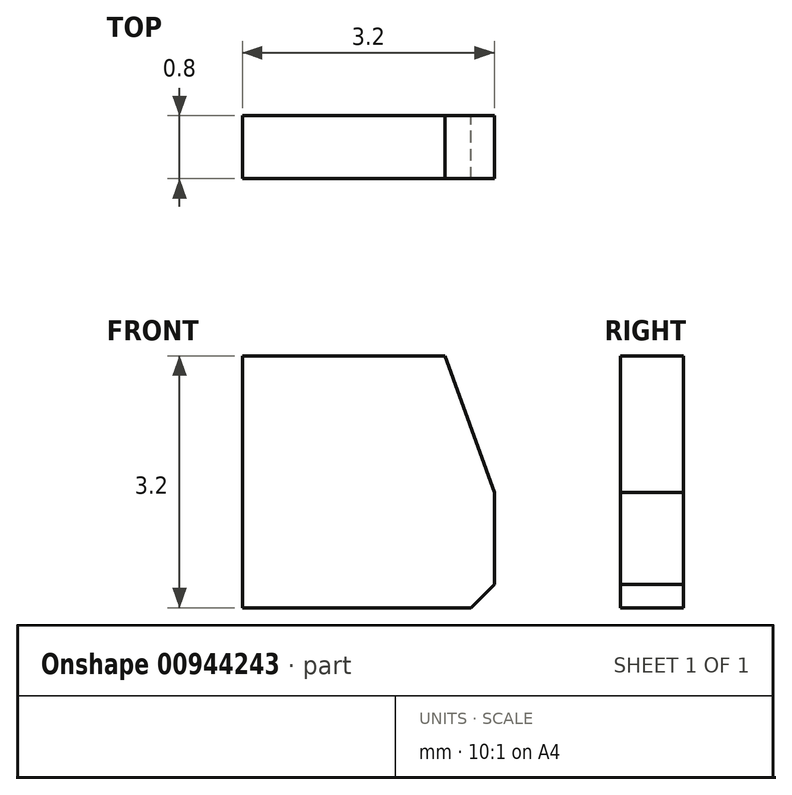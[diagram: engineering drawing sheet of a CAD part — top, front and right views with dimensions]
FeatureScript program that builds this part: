
annotation { "Feature Type Name" : "Feature", "Feature Type Description" : "" }
export const myFeature = defineFeature(function(context is Context, id is Id, definition is map)
    precondition{}
    {
        {
            var Q0;
            Q0=qCreatedBy(makeId("Front.planeOp"),FACE);
            var sketch = newSketch(context, id + "F0", { "sketchPlane" : qUnion([Q0])});
            skLineSegment(sketch, "E0", {"start": v(-2.9, 2.19) * mm, "end": v(-2.9, -1.01) * mm});
            skLineSegment(sketch, "E1", {"start": v(-2.9, -1.01) * mm, "end": v(0, -1.01) * mm});
            skLineSegment(sketch, "E2", {"start": v(0, -1.01) * mm, "end": v(0.3, -0.71) * mm});
            skLineSegment(sketch, "E3", {"start": v(0.3, -0.71) * mm, "end": v(0.3, 0.46) * mm});
            skLineSegment(sketch, "E4", {"start": v(0.3, 0.46) * mm, "end": v(-0.33, 2.19) * mm});
            skLineSegment(sketch, "E5", {"start": v(-0.33, 2.19) * mm, "end": v(-2.9, 2.19) * mm});
            skSolve(sketch);
        }
        {
            var Q0;
            Q0 = qSketchRegion(id + "F0", true);
            extrude(context, id + "F1", {"entities" : qUnion([Q0]), "depth" : 0.8 * mm, "offsetDistance" : 25 * mm});
        }
    });
